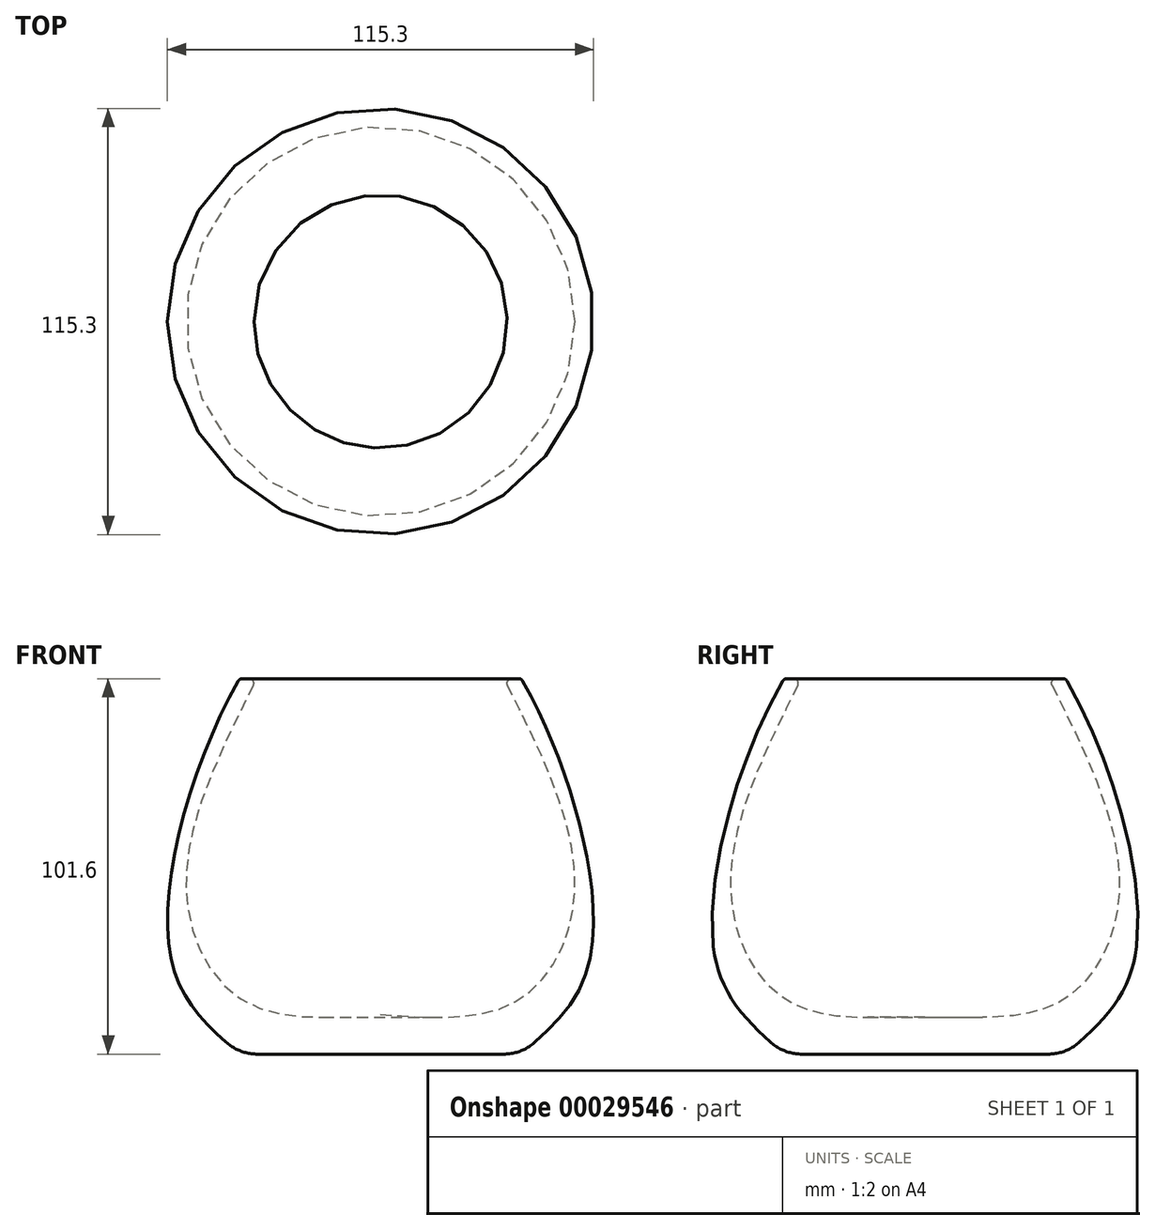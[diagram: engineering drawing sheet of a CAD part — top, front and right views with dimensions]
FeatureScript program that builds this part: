
annotation { "Feature Type Name" : "Feature", "Feature Type Description" : "" }
export const myFeature = defineFeature(function(context is Context, id is Id, definition is map)
    precondition{}
    {
        {
            var Q0;
            Q0=qCreatedBy(makeId("Front.planeOp"),FACE);
            var sketch = newSketch(context, id + "F0", { "sketchPlane" : qUnion([Q0])});
            skLineSegment(sketch, "E0", {"start": v(0, 0) * mm, "end": v(0, 10.73) * mm});
            skLineSegment(sketch, "E1", {"start": v(35.53, 101.6) * mm, "end": v(37.37, 101.6) * mm});
            skFitSpline(sketch, "E2", {"points": [v(38.1, 101.6) * mm, v(57.02, 27.5) * mm, v(38.1, 0) * mm], "startDerivative": vector(61.56, -106.04) * mm, "endDerivative": vector(-66.92, -57.85) * mm});
            skLineSegment(sketch, "E3", {"start": v(0, 0) * mm, "end": v(33.33, 0) * mm});
            skFitSpline(sketch, "E4", {"points": [v(0, 10.73) * mm, v(37.46, 14.72) * mm, v(52.63, 46.25) * mm, v(33.47, 101.6) * mm], "startDerivative": vector(133.18, -9.8) * mm, "endDerivative": vector(-73.98, 146.94) * mm});
            skArc(sketch, "E5.filletArc", {"start": v(35.53, 101.6) * mm, "mid": v(34.45, 101) * mm, "end": v(34.4, 99.76) * mm});
            skArc(sketch, "E6.filletArc", {"start": v(38.47, 100.96) * mm, "mid": v(38, 101.43) * mm, "end": v(37.37, 101.6) * mm});
            skArc(sketch, "E7.filletArc", {"start": v(33.33, 0) * mm, "mid": v(37.86, 0.83) * mm, "end": v(41.8, 3.23) * mm});
            skSolve(sketch);
        }
        {
            var Q0;
            Q0 = qSketchRegion(id + "F0", true);
            var Q1;
            Q1=sQuery(id+"F0.wireOp",EDGE,"E0");
            revolve(context, id + "F1", {"entities" : qUnion([Q0]), "axis" : qUnion([Q1]), "revolveType" : RevolveType.FULL});
        }
    });
